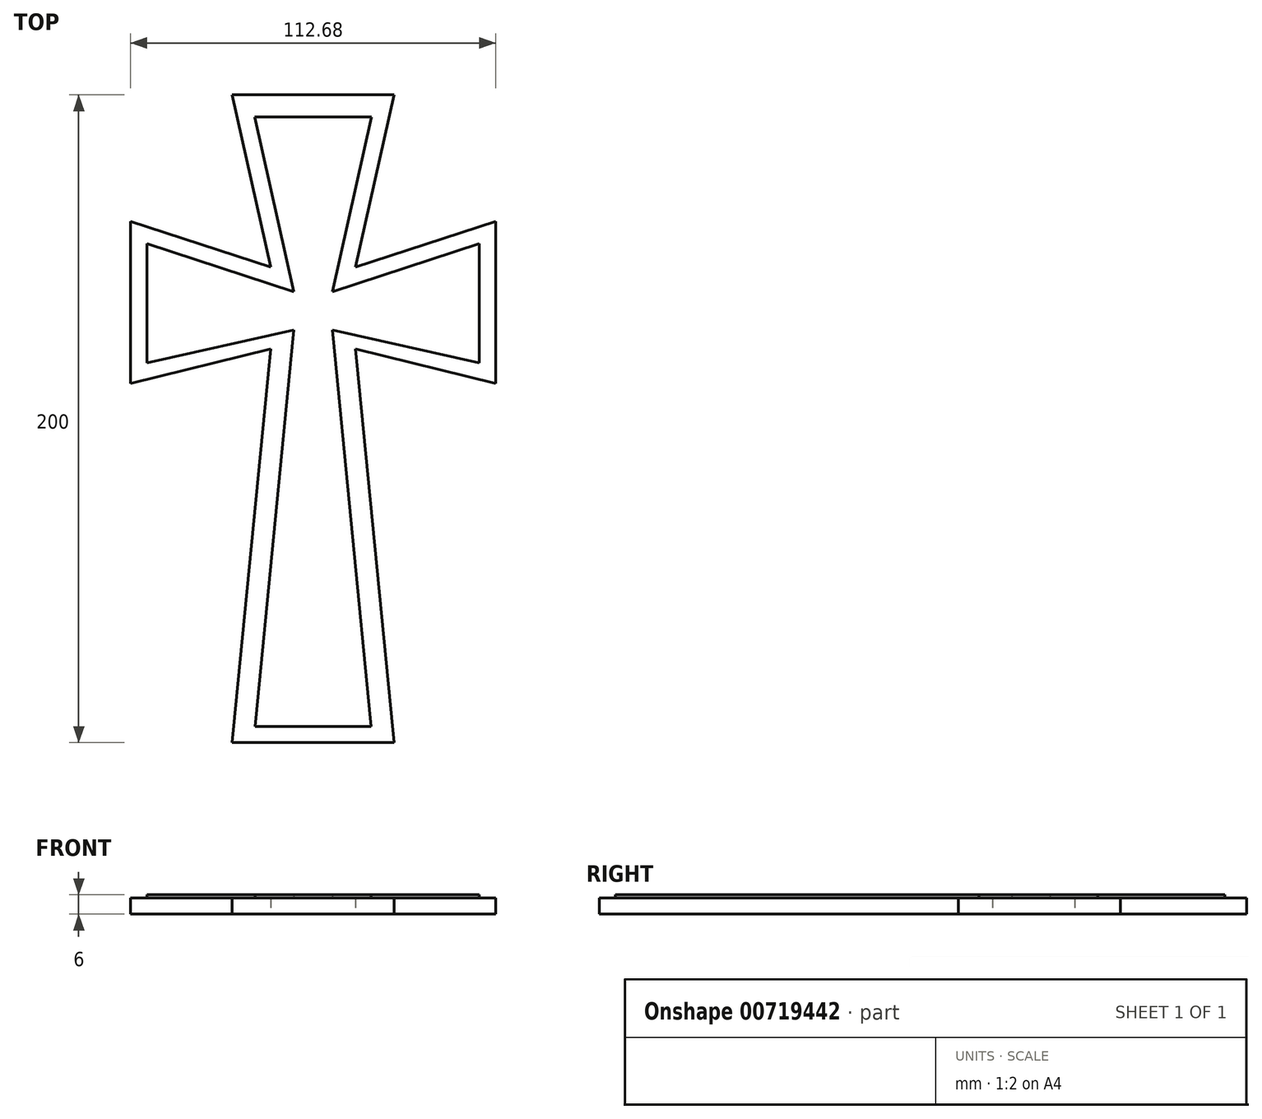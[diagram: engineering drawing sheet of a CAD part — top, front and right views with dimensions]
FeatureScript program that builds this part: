
annotation { "Feature Type Name" : "Feature", "Feature Type Description" : "" }
export const myFeature = defineFeature(function(context is Context, id is Id, definition is map)
    precondition{}
    {
        {
            var Q0;
            Q0=qCreatedBy(makeId("Top.planeOp"),FACE);
            var sketch = newSketch(context, id + "F0", { "sketchPlane" : qUnion([Q0])});
            skLineSegment(sketch, "E0", {"start": v(0, 78.49) * mm, "end": v(25, 78.49) * mm});
            skLineSegment(sketch, "E1", {"start": v(25, 78.49) * mm, "end": v(13.11, 25.31) * mm});
            skLineSegment(sketch, "E2", {"start": v(56.34, 39.4) * mm, "end": v(56.34, -10.6) * mm});
            skLineSegment(sketch, "E3", {"start": v(13.11, 0) * mm, "end": v(25, -121.51) * mm});
            skLineSegment(sketch, "E4", {"start": v(25, -121.51) * mm, "end": v(0, -121.51) * mm});
            skLineSegment(sketch, "E5.MirrorCS", {"start": v(-13.11, 0) * mm, "end": v(-25, -121.51) * mm});
            skLineSegment(sketch, "E6.MirrorCS", {"start": v(-25, -121.51) * mm, "end": v(0, -121.51) * mm});
            skLineSegment(sketch, "E7.MirrorCS", {"start": v(-25, 78.49) * mm, "end": v(-13.11, 25.31) * mm});
            skLineSegment(sketch, "E8.MirrorCS", {"start": v(0, 78.49) * mm, "end": v(-25, 78.49) * mm});
            skLineSegment(sketch, "E9.MirrorCS", {"start": v(-56.34, 39.4) * mm, "end": v(-56.34, -10.6) * mm});
            skLineSegment(sketch, "E10", {"start": v(13.11, 25.31) * mm, "end": v(56.34, 39.4) * mm});
            skLineSegment(sketch, "E11", {"start": v(56.34, -10.6) * mm, "end": v(13.11, 0) * mm});
            skLineSegment(sketch, "E12.MirrorCS", {"start": v(-56.34, -10.6) * mm, "end": v(-13.11, 0) * mm});
            skLineSegment(sketch, "E13.MirrorCS", {"start": v(-13.11, 25.31) * mm, "end": v(-56.34, 39.4) * mm});
            skLineSegment(sketch, "E14", {"start": v(0, 71.72) * mm, "end": v(18.04, 71.72) * mm});
            skLineSegment(sketch, "E15", {"start": v(18.04, 71.72) * mm, "end": v(5.97, 17.73) * mm});
            skLineSegment(sketch, "E16", {"start": v(5.97, 17.73) * mm, "end": v(51.34, 32.52) * mm});
            skLineSegment(sketch, "E17", {"start": v(51.34, 32.52) * mm, "end": v(51.34, -4.22) * mm});
            skLineSegment(sketch, "E18", {"start": v(51.34, -4.22) * mm, "end": v(5.97, 5.92) * mm});
            skLineSegment(sketch, "E19", {"start": v(5.97, 5.92) * mm, "end": v(17.95, -116.51) * mm});
            skLineSegment(sketch, "E20", {"start": v(17.95, -116.51) * mm, "end": v(0, -116.51) * mm});
            skLineSegment(sketch, "E21.MirrorCS", {"start": v(-51.34, -4.22) * mm, "end": v(-5.97, 5.92) * mm});
            skLineSegment(sketch, "E22.MirrorCS", {"start": v(-5.97, 17.73) * mm, "end": v(-51.34, 32.52) * mm});
            skLineSegment(sketch, "E23.MirrorCS", {"start": v(-5.97, 5.92) * mm, "end": v(-17.95, -116.51) * mm});
            skLineSegment(sketch, "E24.MirrorCS", {"start": v(-18.04, 71.72) * mm, "end": v(-5.97, 17.73) * mm});
            skLineSegment(sketch, "E25.MirrorCS", {"start": v(-51.34, 32.52) * mm, "end": v(-51.34, -4.22) * mm});
            skLineSegment(sketch, "E26.MirrorCS", {"start": v(0, 71.72) * mm, "end": v(-18.04, 71.72) * mm});
            skLineSegment(sketch, "E27.MirrorCS", {"start": v(-17.95, -116.51) * mm, "end": v(0, -116.51) * mm});
            skSolve(sketch);
        }
        {
            var Q0;
            Q0=makeQuery(id+"F0.imprint","IMPRINT",FACE,{"disambiguationData":[TD([[makeQuery(id+"F0.imprint","IMPRINT",EDGE,{"derivedFrom":sQuery(id+"F0.wireOp",EDGE,"oTEXQA8a-RtNP-hIsy-bG68-uGz2sJ20PT4r")}),-1.0]])]});
            var Q1;
            Q1=makeQuery(id+"F0.imprint","IMPRINT",FACE,{"disambiguationData":[TD([[makeQuery(id+"F0.imprint","IMPRINT",EDGE,{"derivedFrom":sQuery(id+"F0.wireOp",EDGE,"E0")}),-1.0]])]});
            var Q2;
            Q2=makeQuery(id+"F0.imprint","IMPRINT",FACE,{"disambiguationData":[TD([[makeQuery(id+"F0.imprint","IMPRINT",EDGE,{"derivedFrom":sQuery(id+"F0.wireOp",EDGE,"E14")}),-1.0]])]});
            extrude(context, id + "F1", {"entities" : qUnion([Q0, Q1, Q2]), "depth" : 5 * mm, "offsetDistance" : 25 * mm});
        }
        {
            var Q0;
            Q0=makeQuery(id+"F0.imprint","IMPRINT",FACE,{"disambiguationData":[TD([[makeQuery(id+"F0.imprint","IMPRINT",EDGE,{"derivedFrom":sQuery(id+"F0.wireOp",EDGE,"E14")}),-1.0]])]});
            extrude(context, id + "F2", {"entities" : qUnion([Q0]), "operationType" : NewBodyOperationType.ADD, "depth" : 6 * mm, "offsetDistance" : 25 * mm});
        }
    });
